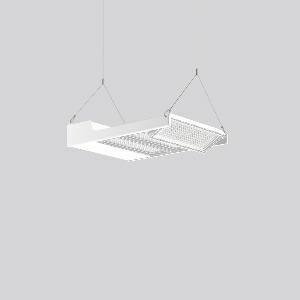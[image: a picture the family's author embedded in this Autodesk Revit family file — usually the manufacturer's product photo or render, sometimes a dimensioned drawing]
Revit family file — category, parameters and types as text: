
# Revit family: light_case_921683_002_76_f192
name_source: partatom
category: Lighting Fixtures
units: mm (PartAtom-declared; Revit-internal decimal feet)

## family parameters
Cut with Voids When Loaded = No
Host = Face
Light Source = No
Part Type = Normal
Room Calculation Point = No
Round Connector Dimension = Use Diameter
Shared = No

## types (1)
- LIGHT CASE (1 x LED Modul 840, 8833.33 lm, 4000)
    Apparent Load = 168 VA
    CIE Flux Codes = 89 96 99 100 100
    Color Rendering = 80
    Color Temperature = 4000
    Default Elevation = 1800 mm
    Description = Series: LIGHT CASE
Flat highbay luminaire for chain or cable suspension with 3 LED modules that can be swivelled. Housing: die cast aluminium and sheet steel, powder-coated. Optimised thermal management thanks to special luminaire design. Self-cleaning heat sink for constant heat dissipation. Cover: plastic (polycarbonate, shockproof), with integrated four-row lens system. LED modules can be swivelled ± 30° for optimum illumination. CLO control for constant light output over the entire service life. Suitable for chain or steel cable suspension (to be provided on site). With 5-pin connection terminal (1.5 m). With integrated movement sensor and light sensor for daylight detection on request. Ball impact proof in accordance with DIN 18032-03 (except steel cable suspension). Luminaire with limited surface temperature in accordance with EN 60598-2-24 for use in environments in which a deposit of conductive dust on the luminaire can be expected. 
Colour: white
Length: 544 mm
Width: 397 mm
Height: 110 mm
Lamp: LED
Socket: without socket
Colour temperature: 4000K
Colour rendering index (CRI): 80
System power: 168 W
Rated luminous flux: 26500 lm
Luminous efficiency: 158 lm/W
Control gear: Converter, dimmable, DALI
Protection class: I
Type of protection: IP 65
    Height = 110 mm
    Lamp = 1 x LED Modul 840
    Lamp Light Flux = 8833.33 lm
    Lamp count = 1
    Length = 544 mm
    Lifetime = 50000 h
    Luminous efficacy = 158 lm/W
    Manufacturer = RZB
    ModVariant = No
    Model = 921683.002.76
    Mounting Place = Ceiling
    Mounting Type = Pendant
    Number of Poles = 1
    OnlyDefault = Yes
    Power Factor = 1
    Product Name = LIGHT CASE
    Product group = Pendant commercial luminaires
    ProductGroupID = 903
    Protection Class = Protection class I
    Protection Degree = IP 65
    RLX_Detail_Level = 1
    RLX_Emergency_Light_Flux = 0 lm
    RLX_Emergency_Type = 0
    RLX_Emergency_Type_DB = No
    RlxData = <blob elided: 26381 chars, md5=45ff71e7>
    Socket = socket
    Standby Power = 0 W
    System Light Flux = 26500 lm
    System Power = 168 W
    Type Comments = Product without accessories
    Type Image = 921520.002.76.jpg
    URL = http://relux.com
    VarID = ---
    Voltage = 230 V
    Voltage Range = 220-240 V
    Weight = 0.00 kg
    Width = 397 mm

## geometry (parser evidence)
native form markers: Blend x4, Sweep x18
no freeform markers — native parametric forms only
